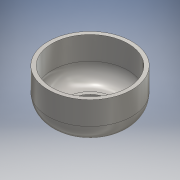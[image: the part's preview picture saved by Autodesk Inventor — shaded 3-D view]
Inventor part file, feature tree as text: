
AUTODESK INVENTOR PART (.ipt)
format: ipt  version: 2016 (Build 200138000, 138)  size: 258,048 bytes
history: native  units: mm
features: sketch x7, extrude x4, pattern_circular x3, projected_geometry x3, other x2, revolve x2, mirror x2, reference x2, thicken_offset x1, fillet x1, plane x1, hole x1
ambient origin geometry x8: Origin, YZ Plane, XZ Plane, XY Plane, X Axis, Y Axis, Z Axis, Center Point
bodies: Solid1 (feature_tree)
feature tree (29):
  other  "Fixture.ipt"
  other  "Transmission.ipt"
  revolve  "Revolution1"  [1 undecoded]
  sketch  "Sketch3"  dims[d4=3.0mm d5=90.0deg]
  extrude  "Extrusion1"  Depth=75.6mm
  extrude  "Extrusion2"  TaperAngle=90.0deg  [1 undecoded]
  mirror  "Mirror3"
  extrude  "Extrusion3"  Depth=10.0mm
  pattern_circular  "Circular Pattern1"  [2 undecoded]
  thicken_offset  "Thicken1"
  fillet  "Fillet1"  [1 undecoded]
  plane  "Work Plane3"
  hole  "Hole2"  [1 undecoded]
  revolve  "Revolution2"  [1 undecoded]
  sketch  "Sketch10"  dims[d9=22.2mm]
  pattern_circular  "Circular Pattern3"  Count=2 Angle=360.0deg
  pattern_circular  "Circular Pattern4"  [2 undecoded]
  mirror  "Mirror2"
  extrude  "Extrusion4"  Depth=0.1mm
  sketch  "Sketch1"  dims[d0=10.0mm d1=76.5mm]
  sketch  "Sketch2"  dims[d2=41.3mm d3=75.6mm]
  projected_geometry  "Projected Loop3"
  sketch  "Sketch4"  dims[d7=50.9mm d8=10.0mm]
  reference  "Reference1"
  sketch  "Sketch11"  dims[d10=0.0mm]
  sketch  "Sketch12"  dims[d11=2.0mm d12=22.2mm d13=0.0mm d15=26.7mm d16=0.0mm d17=20.0mm d18=360.0deg d20=0.1mm d21=0.1mm d22=3.0mm d38=9.0mm d39=26.7mm d40=0.0mm d42=4.5mm d44=5.0mm d45=20.0mm d46=90.0deg d48=2.0mm d49=6.0mm d50=4.0mm d51=2.0mm d52=90.0deg d53=8.0mm d54=20.594885mm d55=30.0mm d56=11.524164mm d58=30.0mm d59=11.524164mm]
  projected_geometry  "Projected Loop7"
  projected_geometry  "Projected Loop8"
  reference  "Reference4"
note: 9 required parameter values undecoded (feature->parameter linkage not recoverable at this tier; creation-order binding heuristic only, values carry confidence <= 0.55)